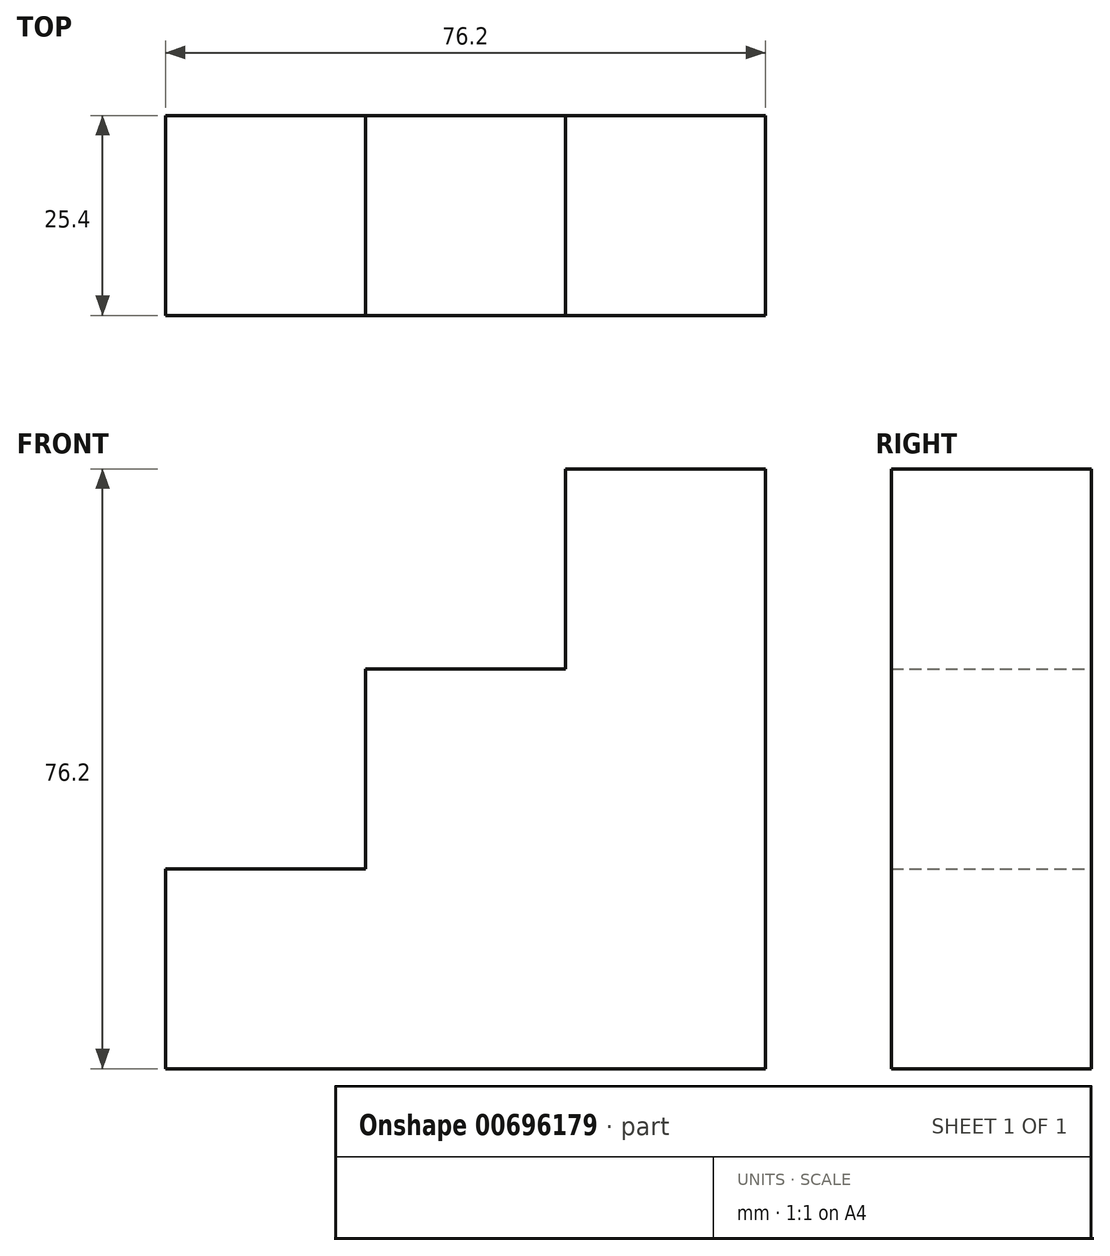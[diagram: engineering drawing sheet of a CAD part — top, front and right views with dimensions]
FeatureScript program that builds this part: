
annotation { "Feature Type Name" : "Feature", "Feature Type Description" : "" }
export const myFeature = defineFeature(function(context is Context, id is Id, definition is map)
    precondition{}
    {
        {
            var Q0;
            Q0=qCreatedBy(makeId("Front.planeOp"),FACE);
            var sketch = newSketch(context, id + "F0", { "sketchPlane" : qUnion([Q0])});
            skLineSegment(sketch, "E0", {"start": v(-25.4, 25.4) * mm, "end": v(-25.4, 0) * mm});
            skLineSegment(sketch, "E1", {"start": v(-25.4, 0) * mm, "end": v(50.8, 0) * mm});
            skLineSegment(sketch, "E2", {"start": v(50.8, 0) * mm, "end": v(50.8, 76.2) * mm});
            skLineSegment(sketch, "E3", {"start": v(50.8, 76.2) * mm, "end": v(25.4, 76.2) * mm});
            skLineSegment(sketch, "E4", {"start": v(25.4, 76.2) * mm, "end": v(25.4, 50.8) * mm});
            skLineSegment(sketch, "E5", {"start": v(25.4, 50.8) * mm, "end": v(0, 50.8) * mm});
            skLineSegment(sketch, "E6", {"start": v(0, 50.8) * mm, "end": v(0, 25.4) * mm});
            skLineSegment(sketch, "E7", {"start": v(0, 25.4) * mm, "end": v(-25.4, 25.4) * mm});
            skSolve(sketch);
        }
        {
            var Q0;
            Q0=makeQuery(id+"F0.imprint","IMPRINT",FACE,{"disambiguationData":[TD([[makeQuery(id+"F0.imprint","IMPRINT",EDGE,{"derivedFrom":sQuery(id+"F0.wireOp",EDGE,"E0")}),1.0]])]});
            extrude(context, id + "F1", {"entities" : qUnion([Q0]), "depth" : 25.4 * mm, "offsetDistance" : 25.4 * mm});
        }
    });
